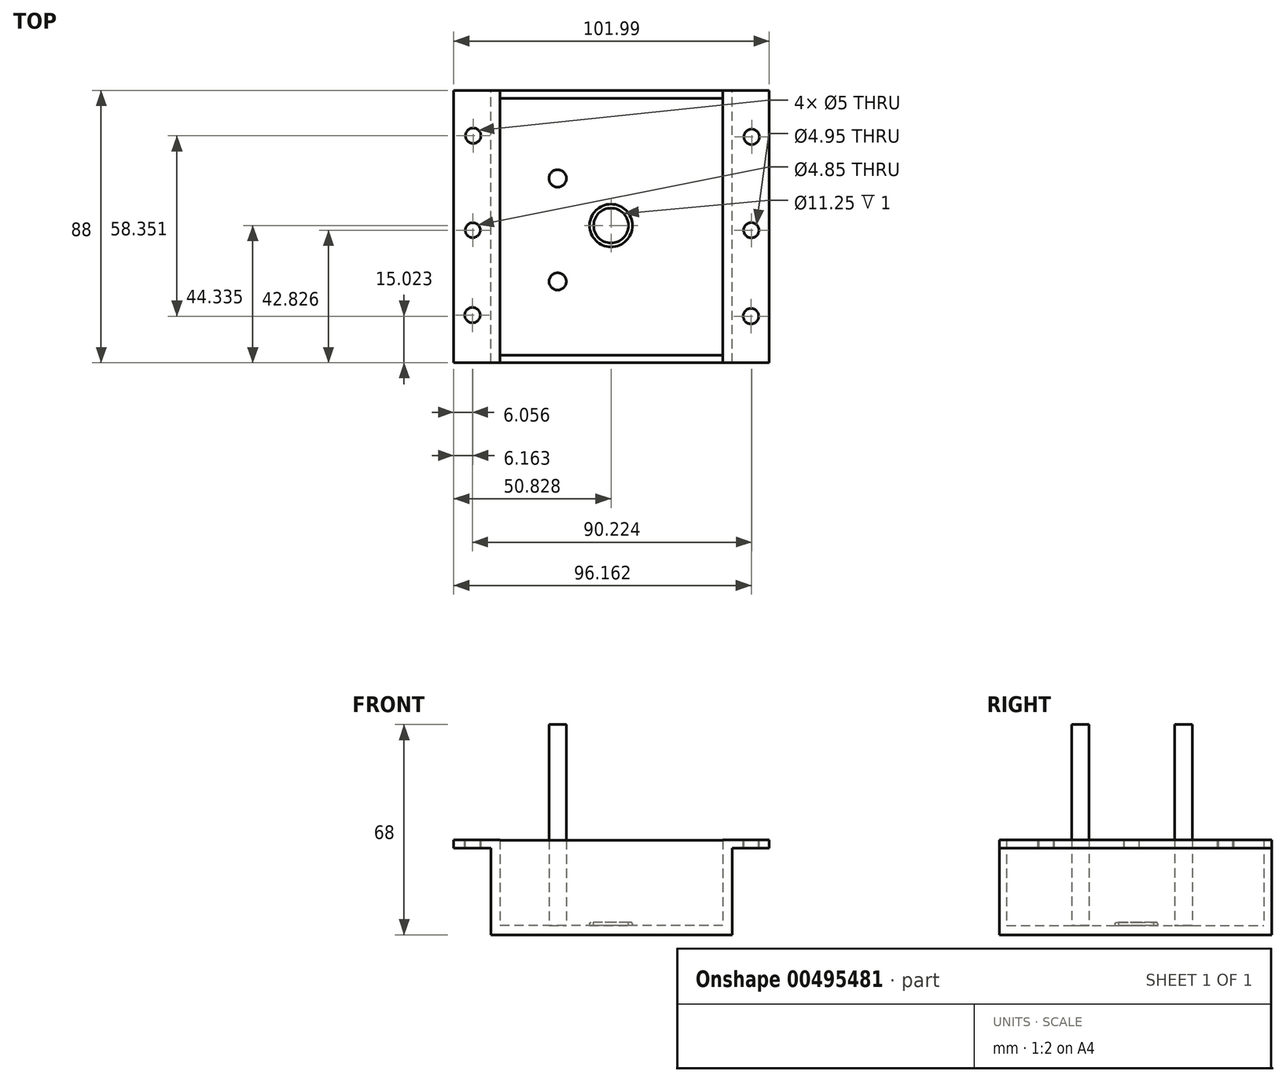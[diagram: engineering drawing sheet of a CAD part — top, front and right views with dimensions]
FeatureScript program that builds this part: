
annotation { "Feature Type Name" : "Feature", "Feature Type Description" : "" }
export const myFeature = defineFeature(function(context is Context, id is Id, definition is map)
    precondition{}
    {
        {
            var Q0;
            Q0=qCreatedBy(makeId("Front.planeOp"),FACE);
            var sketch = newSketch(context, id + "F0", { "sketchPlane" : qUnion([Q0])});
            skLineSegment(sketch, "E0", {"start": v(-2.97, -6.62) * mm, "end": v(-2.97, -9.62) * mm});
            skLineSegment(sketch, "E1", {"start": v(-2.97, -9.62) * mm, "end": v(36.03, -9.62) * mm});
            skLineSegment(sketch, "E2", {"start": v(36.03, -9.62) * mm, "end": v(36.03, 18.38) * mm});
            skLineSegment(sketch, "E3", {"start": v(36.03, 18.38) * mm, "end": v(48.02, 18.38) * mm});
            skLineSegment(sketch, "E4", {"start": v(48.02, 18.38) * mm, "end": v(48.02, 21.12) * mm});
            skLineSegment(sketch, "E5", {"start": v(48.02, 21.12) * mm, "end": v(33.02, 21.12) * mm});
            skLineSegment(sketch, "E6", {"start": v(33.02, 21.12) * mm, "end": v(33.02, -6.62) * mm});
            skLineSegment(sketch, "E7", {"start": v(33.02, -6.62) * mm, "end": v(-2.97, -6.62) * mm});
            skLineSegment(sketch, "E8.MirrorCS", {"start": v(-53.97, 18.38) * mm, "end": v(-53.97, 21.12) * mm});
            skLineSegment(sketch, "E9.MirrorCS", {"start": v(-41.97, -9.62) * mm, "end": v(-41.97, 18.38) * mm});
            skLineSegment(sketch, "E10.MirrorCS", {"start": v(-41.97, 18.38) * mm, "end": v(-53.97, 18.38) * mm});
            skLineSegment(sketch, "E11.MirrorCS", {"start": v(-53.97, 21.12) * mm, "end": v(-38.97, 21.12) * mm});
            skLineSegment(sketch, "E12.MirrorCS", {"start": v(-38.97, 21.12) * mm, "end": v(-38.97, -6.62) * mm});
            skLineSegment(sketch, "E13.MirrorCS", {"start": v(-2.97, -9.62) * mm, "end": v(-41.97, -9.62) * mm});
            skLineSegment(sketch, "E14.MirrorCS", {"start": v(-38.97, -6.62) * mm, "end": v(-2.97, -6.62) * mm});
            skPoint(sketch, "E15.MirrorCS.start.orphan", {"position": v(36.03, 18.38) * mm});
            skSolve(sketch);
        }
        {
            var Q0;
            Q0=qSketchRegion(id+"F0",true);
            extrude(context, id + "F1", {"entities" : qUnion([Q0]), "endBound" : BoundingType.SYMMETRIC, "depth" : 88 * mm});
        }
        {
            var Q0;
            Q0=makeQuery(id+"F1.opExtrude","SWEPT_FACE",FACE,{"disambiguationData":[OSD([sQuery(id+"F0.wireOp",EDGE,"E5")])]});
            var sketch = newSketch(context, id + "F2", { "sketchPlane" : qUnion([Q0])});
            skLineSegment(sketch, "E16", {"start": v(42.02, -44) * mm, "end": v(42.33, 34) * mm, "construction": true});
            skLineSegment(sketch, "E17.0.0", {"start": v(-38.97, 44) * mm, "end": v(-53.97, 44) * mm, "construction": true});
            skLineSegment(sketch, "E17.0.1", {"start": v(-53.97, 44) * mm, "end": v(-53.97, -44) * mm, "construction": true});
            skLineSegment(sketch, "E17.0.2", {"start": v(-53.97, -44) * mm, "end": v(-38.97, -44) * mm, "construction": true});
            skLineSegment(sketch, "E17.0.3", {"start": v(-38.97, -44) * mm, "end": v(-38.97, 44) * mm, "construction": true});
            skLineSegment(sketch, "E18", {"start": v(-47.67, 34) * mm, "end": v(-47.97, -44) * mm, "construction": true});
            skLineSegment(sketch, "E19", {"start": v(-53.97, -28.6) * mm, "end": v(48.02, -29) * mm, "construction": true});
            skLineSegment(sketch, "E20", {"start": v(48.02, 29) * mm, "end": v(-53.97, 29.4) * mm, "construction": true});
            skLineSegment(sketch, "E21", {"start": v(48.02, -29) * mm, "end": v(48.02, -44) * mm, "construction": true});
            skLineSegment(sketch, "E22", {"start": v(48.02, 44) * mm, "end": v(48.02, 29) * mm, "construction": true});
            skCircle(sketch, "E23", {"center": v(42.08, -28.98) * mm, "radius": 2.5 * mm});
            skCircle(sketch, "E24", {"center": v(42.31, 29.02) * mm, "radius": 2.5 * mm});
            skCircle(sketch, "E25", {"center": v(-47.69, 29.37) * mm, "radius": 2.5 * mm});
            skCircle(sketch, "E26", {"center": v(-47.91, -28.63) * mm, "radius": 2.5 * mm});
            skCircle(sketch, "E27", {"center": v(42.2, -1.17) * mm, "radius": 2.47 * mm});
            skCircle(sketch, "E28", {"center": v(-47.8, -1.17) * mm, "radius": 2.43 * mm});
            skSolve(sketch);
        }
        {
            var Q0;
            Q0=qSketchRegion(id+"F2",true);
            extrude(context, id + "F3", {"entities" : qUnion([Q0]), "operationType" : NewBodyOperationType.REMOVE, "endBound" : BoundingType.UP_TO_NEXT, "oppositeDirection" : true, "depth" : 25 * mm});
        }
        {
            var Q0;
            Q0=makeQuery(id+"F1.opExtrude","SWEPT_FACE",FACE,{"disambiguationData":[OSD([sQuery(id+"F0.wireOp",EDGE,"E7"),sQuery(id+"F0.wireOp",EDGE,"E14.MirrorCS")])]});
            var sketch = newSketch(context, id + "F4", { "sketchPlane" : qUnion([Q0])});
            skLineSegment(sketch, "E29.bottom", {"start": v(33.02, 44) * mm, "end": v(-38.97, 44) * mm});
            skLineSegment(sketch, "E29.top", {"start": v(33.02, 41.5) * mm, "end": v(-38.97, 41.5) * mm});
            skLineSegment(sketch, "E29.left", {"start": v(33.02, 44) * mm, "end": v(33.02, 41.5) * mm});
            skLineSegment(sketch, "E29.right", {"start": v(-38.97, 44) * mm, "end": v(-38.97, 41.5) * mm});
            skLineSegment(sketch, "E30.bottom", {"start": v(33.02, -44) * mm, "end": v(-38.97, -44) * mm});
            skLineSegment(sketch, "E30.top", {"start": v(33.02, -41.63) * mm, "end": v(-38.97, -41.63) * mm});
            skLineSegment(sketch, "E30.left", {"start": v(33.02, -44) * mm, "end": v(33.02, -41.63) * mm});
            skLineSegment(sketch, "E30.right", {"start": v(-38.97, -44) * mm, "end": v(-38.97, -41.63) * mm});
            skSolve(sketch);
        }
        {
            var Q0;
            Q0 = qSketchRegion(id + "F4", true);
            extrude(context, id + "F5", {"entities" : qUnion([Q0]), "operationType" : NewBodyOperationType.ADD, "depth" : 27.6 * mm});
        }
        {
            var Q0;
            Q0=makeQuery(id+"F1.opExtrude","SWEPT_FACE",FACE,{"disambiguationData":[OSD([sQuery(id+"F0.wireOp",EDGE,"E7"),sQuery(id+"F0.wireOp",EDGE,"E14.MirrorCS")])]});
            var sketch = newSketch(context, id + "F6", { "sketchPlane" : qUnion([Q0])});
            skCircle(sketch, "E31", {"center": v(-3.14, 0.33) * mm, "radius": 6.92 * mm});
            skSolve(sketch);
        }
        {
            var Q0;
            Q0 = qSketchRegion(id + "F6", true);
            extrude(context, id + "F7", {"entities" : qUnion([Q0]), "operationType" : NewBodyOperationType.ADD, "depth" : 1 * mm});
        }
        {
            var Q0;
            Q0=makeQuery(id+"F7.opExtrude","CAP_FACE",FACE,{"disambiguationData":[OSD([sQuery(id+"F6.wireOp",EDGE,"E31")])],"isStart":false});
            var sketch = newSketch(context, id + "F8", { "sketchPlane" : qUnion([Q0])});
            skCircle(sketch, "E32", {"center": v(-3.14, 0.33) * mm, "radius": 5.63 * mm});
            skSolve(sketch);
        }
        {
            var Q0;
            Q0 = qSketchRegion(id + "F8", true);
            extrude(context, id + "F9", {"entities" : qUnion([Q0]), "operationType" : NewBodyOperationType.REMOVE, "oppositeDirection" : true, "depth" : 1 * mm});
        }
        {
            var Q0;
            Q0=makeQuery(id+"F7.opExtrude","CAP_EDGE",EDGE,{"disambiguationData":[OSD([sQuery(id+"F6.wireOp",EDGE,"E31")])],"isStart":false});
            var Q1;
            Q1=makeQuery(id+"F9.boolean.opBoolean","COPY",EDGE,{"derivedFrom":makeQuery(id+"F9.opExtrude","CAP_EDGE",EDGE,{"disambiguationData":[OSD([sQuery(id+"F8.wireOp",EDGE,"E32")])],"isStart":true})});
            fillet(context, id + "F10", {"entities" : qUnion([Q0, Q1]), "radius" : 0.5 * mm, "tangentPropagation" : true, "allowEdgeOverflow" : false});
        }
        {
            var Q0;
            Q0=makeQuery(id+"F1.opExtrude","SWEPT_FACE",FACE,{"disambiguationData":[OSD([sQuery(id+"F0.wireOp",EDGE,"E7"),sQuery(id+"F0.wireOp",EDGE,"E14.MirrorCS")])]});
            var sketch = newSketch(context, id + "F11", { "sketchPlane" : qUnion([Q0])});
            skCircle(sketch, "E33", {"center": v(-20.38, 15.57) * mm, "radius": 2.83 * mm});
            skCircle(sketch, "E34", {"center": v(-20.38, -17.74) * mm, "radius": 2.79 * mm});
            skSolve(sketch);
        }
        {
            var Q0;
            Q0 = qSketchRegion(id + "F11", true);
            extrude(context, id + "F12", {"entities" : qUnion([Q0]), "operationType" : NewBodyOperationType.ADD, "depth" : 65 * mm});
        }
    });
